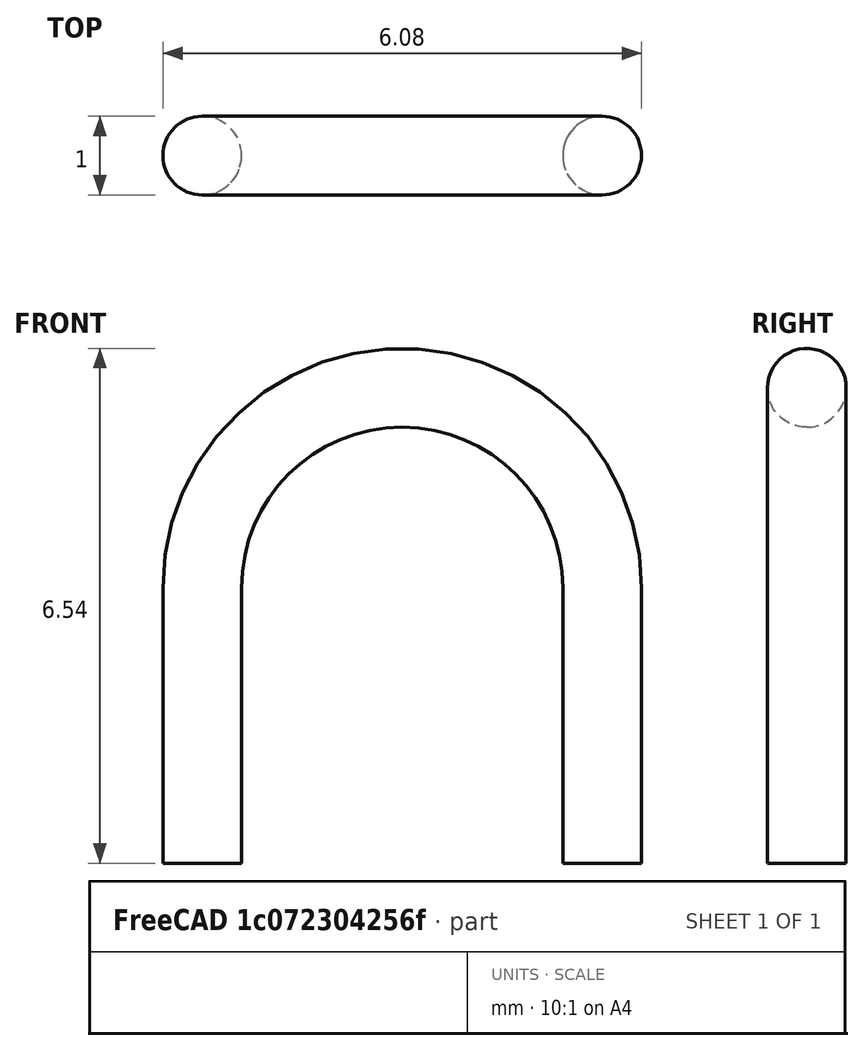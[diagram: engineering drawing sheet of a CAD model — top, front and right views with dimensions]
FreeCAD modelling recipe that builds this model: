
FCSTD DOCUMENT  (FreeCAD 0.17R12018 (Git))
Label: Test_Point_Bridge_Pitch5.08mm_Drill1.3mm
License: All rights reserved
LicenseURL: http://en.wikipedia.org/wiki/All_rights_reserved
objects: Sketcher::SketchObject×2, Spreadsheet::Sheet×1, PartDesign::SubtractivePipe×1, PartDesign::Body×1
note: 5 computed .brp shape members not serialized (recipe doc carries the construction recipe); baked Part::Feature solids carry a one-line shape summary decoded from their .brp

FEATURE [Sketcher::SketchObject] Sketch
  MapMode = 5
  Placement = pos=(0,0,-3) rot=(0,0,1;0rad)
  Support = -> [XY_Plane]
  superPlacement = pos=(0,0,-3) rot=(0,0,1;0rad)
  expr: Constraints[1] = dims.DWire / 2
  sketch-geometry (1):
    g0: Circle CenterX=0 CenterY=0 CenterZ=0 NormalX=0 NormalY=0 NormalZ=1 Radius=0.5
  constraints (2):
    c: Coincident(g0,g-1)
    c: Radius(g0) = 0.5
FEATURE [Spreadsheet::Sheet] Spreadsheet  label="dims"
  cells = A1="DWire"; B1(DWire)=1; A2="Pitch"; B2(Pitch)=5.0800000000000001
FEATURE [Sketcher::SketchObject] Sketch001
  MapMode = 5
  Placement = pos=(0,0,0) rot=(1,0,0;1.5708rad)
  Support = -> [XZ_Plane]
  expr: Constraints[10] = dims.DWire / 2
  expr: Constraints[3] = dims.Pitch
  sketch-geometry (4):
    g0: LineSegment StartX=0 StartY=-3 StartZ=0 EndX=0 EndY=0.5 EndZ=0
    g1: LineSegment StartX=5.08 StartY=0.5 StartZ=0 EndX=5.08 EndY=-3 EndZ=0
    g2: LineSegment [constr] StartX=0 StartY=0.5 StartZ=0 EndX=5.08 EndY=0.5 EndZ=0
    g3: ArcOfCircle CenterX=2.54 CenterY=0.5 CenterZ=0 NormalX=0 NormalY=0 NormalZ=1 Radius=2.54 StartAngle=0 EndAngle=3.14159
  constraints (13):
    c: PointOnObject(g0,g-2)
    c: Vertical(g0)
    c: Vertical(g1)
    c: DistanceX(g0,g1) = 5.08
    c: Coincident(g2,g0)
    c: Coincident(g2,g1)
    c: Horizontal(g2)
    c: PointOnObject(g3,g2)
    c: Coincident(g3,g0)
    c: Coincident(g3,g1)
    c: DistanceY(g-1,g3) = 0.5
    c: DistanceY(g0,g-1) = 3
    c: Equal(g1,g0)
FEATURE [PartDesign::SubtractivePipe] SubtractivePipe
  AuxilleryCurvelinear = true
  AuxillerySpineTangent = false
  Binormal = (0,0,0)
  Mode = 0
  Profile = -> Sketch
  Spine = -> Sketch001
  SpineTangent = false
  Transformation = 0
  Transition = 0
FEATURE [PartDesign::Body] Body  label="Test_Point_Bridge_Pitch5.08mm_Drill1.3mm"
  Group = -> [Sketch,Sketch001,SubtractivePipe]
  Origin = -> Origin
  Tip = -> SubtractivePipe
